# Revit family: 846906W CARE 660 CF WFCC EH BE PAN+ARH
name_source: partatom
category: Plumbing Fixtures
revit_build: Autodesk Revit 2016 (Build: 20161004_0715(x64)
units: mm (PartAtom-declared; Revit-internal decimal feet)

## family parameters
Cut with Voids When Loaded = No
Host = Face
OmniClass Number = 23.45.05.21.11.11
OmniClass Title = Water Operated Water Closets
Part Type = Normal
Room Calculation Point = No
Round Connector Dimension = Use Diameter
Shared = No

## types (4) — shared parameters
Assembly Code = D2010110
CW Connection = Yes
HW Connection = No
Manufacturer = GWA Bathrooms & Kitchens
Material_Pan = GWA-Porcelain-White
URL = https://www.caroma.com.au
Vent Connection = No
Waste Connection = Yes
zero-valued in all types: Default Elevation

## per-type parameters (varying)
| type | ARH-Hole | ARH-Left | ARH-Right | BI-Hole | BI-Void-Left | BI-Void-Right | Model |
| CARE 660 CF WF CC EH 4S BE PAN | No | 1 mm  [stored 0.00328084 ft] | 0 mm  [stored 0 ft] | No | 1 mm  [stored 0.00328084 ft] | 0 mm  [stored 0 ft] | 846905W |
| CARE 660 CF WFCC EH BE PAN+ARH | Yes | 160 mm  [stored 0.524934 ft] | -160 mm  [stored -0.524934 ft] | No | 1 mm  [stored 0.00328084 ft] | 0 mm  [stored 0 ft] | 846906W |
| CARE 660 CF WF CC EH 4S BI PAN | No | 1 mm  [stored 0.00328084 ft] | 0 mm  [stored 0 ft] | Yes | 160 mm  [stored 0.524934 ft] | -160 mm  [stored -0.524934 ft] | 846915W |
| CARE 660 CF WFCC EH BI PAN+ARH | Yes | 160 mm  [stored 0.524934 ft] | -160 mm  [stored -0.524934 ft] | Yes | 160 mm  [stored 0.524934 ft] | -160 mm  [stored -0.524934 ft] | 846916W |

note: column(s) folded — value = type name in every type: Description

note: [stored X ft] marks values corroborated as IEEE doubles in the binary element streams (Revit-internal decimal feet)

## geometry (parser evidence)
native form markers: Sweep x2
no freeform markers — native parametric forms only
